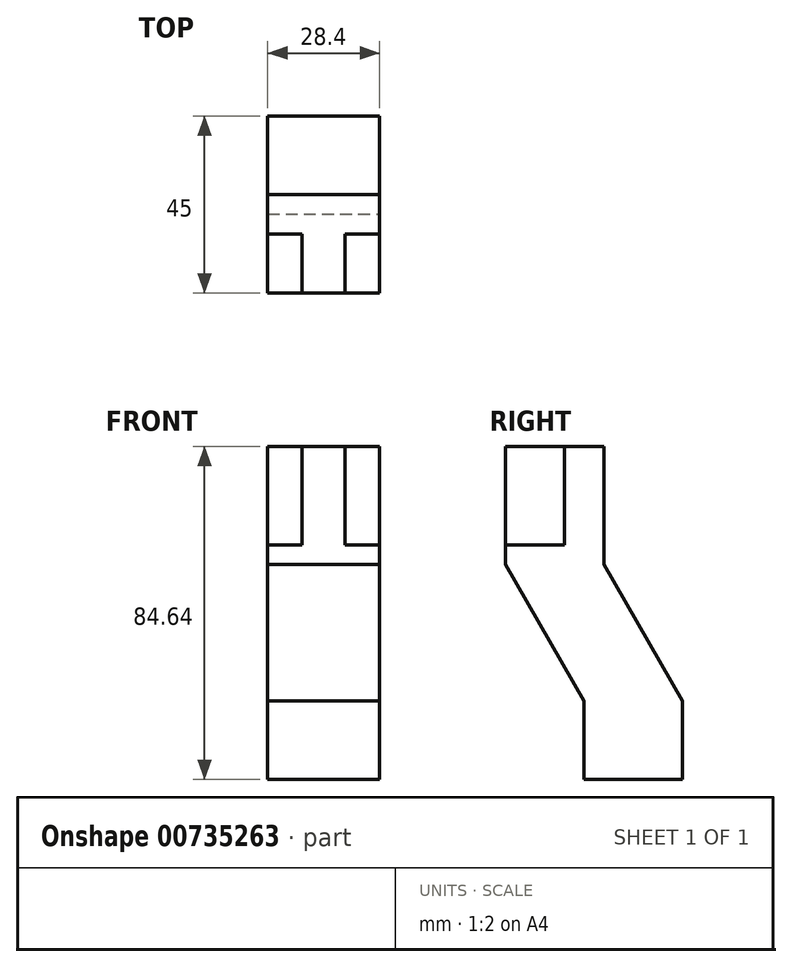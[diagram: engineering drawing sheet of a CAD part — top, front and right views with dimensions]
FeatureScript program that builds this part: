
annotation { "Feature Type Name" : "Feature", "Feature Type Description" : "" }
export const myFeature = defineFeature(function(context is Context, id is Id, definition is map)
    precondition{}
    {
        {
            var Q0;
            Q0=qCreatedBy(makeId("Top.planeOp"),FACE);
            var sketch = newSketch(context, id + "F0", { "sketchPlane" : qUnion([Q0])});
            skLineSegment(sketch, "E0", {"start": v(-5.5, -12.5) * mm, "end": v(5.5, -12.5) * mm});
            skLineSegment(sketch, "E1", {"start": v(5.5, -12.5) * mm, "end": v(5.5, 2.5) * mm});
            skLineSegment(sketch, "E2", {"start": v(5.5, 2.5) * mm, "end": v(14.2, 2.5) * mm});
            skLineSegment(sketch, "E3", {"start": v(14.2, 2.5) * mm, "end": v(14.2, 12.5) * mm});
            skLineSegment(sketch, "E4", {"start": v(14.2, 12.5) * mm, "end": v(-14.2, 12.5) * mm});
            skLineSegment(sketch, "E5", {"start": v(-14.2, 12.5) * mm, "end": v(-14.2, 2.5) * mm});
            skLineSegment(sketch, "E6", {"start": v(-14.2, 2.5) * mm, "end": v(-5.5, 2.5) * mm});
            skLineSegment(sketch, "E7", {"start": v(-5.5, 2.5) * mm, "end": v(-5.5, -12.5) * mm});
            skSolve(sketch);
        }
        {
            var Q0;
            Q0=makeQuery(id+"F0.imprint","IMPRINT",FACE,{"disambiguationData":[TD([[makeQuery(id+"F0.imprint","IMPRINT",EDGE,{"derivedFrom":sQuery(id+"F0.wireOp",EDGE,"E0")}),1.0]])]});
            extrude(context, id + "F1", {"entities" : qUnion([Q0]), "oppositeDirection" : true, "depth" : 25 * mm});
        }
        {
            var Q0;
            Q0=makeQuery(id+"F1.opExtrude","CAP_FACE",FACE,{"disambiguationData":[OSD([sQuery(id+"F0.wireOp",EDGE,"E0"),sQuery(id+"F0.wireOp",EDGE,"E1"),sQuery(id+"F0.wireOp",EDGE,"E2"),sQuery(id+"F0.wireOp",EDGE,"E3"),sQuery(id+"F0.wireOp",EDGE,"E4"),sQuery(id+"F0.wireOp",EDGE,"E5"),sQuery(id+"F0.wireOp",EDGE,"E6"),sQuery(id+"F0.wireOp",EDGE,"E7")])],"isStart":false});
            var sketch = newSketch(context, id + "F2", { "sketchPlane" : qUnion([Q0])});
            skLineSegment(sketch, "E8.bottom", {"start": v(-14.2, 12.5) * mm, "end": v(14.2, 12.5) * mm});
            skLineSegment(sketch, "E8.top", {"start": v(-14.2, -12.5) * mm, "end": v(14.2, -12.5) * mm});
            skLineSegment(sketch, "E8.left", {"start": v(-14.2, 12.5) * mm, "end": v(-14.2, -12.5) * mm});
            skLineSegment(sketch, "E8.right", {"start": v(14.2, 12.5) * mm, "end": v(14.2, -12.5) * mm});
            skSolve(sketch);
        }
        {
            var Q0;
            Q0=qSketchRegion(id+"F2",true);
            extrude(context, id + "F3", {"entities" : qUnion([Q0]), "operationType" : NewBodyOperationType.ADD, "depth" : 5 * mm});
        }
        {
            var Q0;
            Q0=makeQuery(id+"F3.boolean.opBoolean","MERGE",FACE,{"derivedFrom":[makeQuery(id+"F1.opExtrude","SWEPT_FACE",FACE,{"disambiguationData":[OSD([sQuery(id+"F0.wireOp",EDGE,"E3")])]}),makeQuery(id+"F3.opExtrude","SWEPT_FACE",FACE,{"disambiguationData":[OSD([sQuery(id+"F2.wireOp",EDGE,"E8.right")])]})]});
            var sketch = newSketch(context, id + "F4", { "sketchPlane" : qUnion([Q0])});
            skLineSegment(sketch, "E9", {"start": v(12.5, -30) * mm, "end": v(-12.5, -30) * mm});
            skLineSegment(sketch, "E10", {"start": v(-12.5, -30) * mm, "end": v(7.5, -64.64) * mm});
            skLineSegment(sketch, "E11", {"start": v(7.5, -64.64) * mm, "end": v(7.5, -84.64) * mm});
            skLineSegment(sketch, "E12", {"start": v(7.5, -84.64) * mm, "end": v(32.5, -84.64) * mm});
            skLineSegment(sketch, "E13", {"start": v(32.5, -84.64) * mm, "end": v(32.5, -64.64) * mm});
            skLineSegment(sketch, "E14", {"start": v(32.5, -64.64) * mm, "end": v(12.5, -30) * mm});
            skSolve(sketch);
        }
        {
            var Q0;
            Q0=makeQuery(id+"F4.imprint","IMPRINT",FACE,{"disambiguationData":[TD([[makeQuery(id+"F4.imprint","IMPRINT",EDGE,{"derivedFrom":sQuery(id+"F4.wireOp",EDGE,"E9")}),-1.0]])]});
            extrude(context, id + "F5", {"entities" : qUnion([Q0]), "operationType" : NewBodyOperationType.ADD, "oppositeDirection" : true, "depth" : 28.4 * mm});
        }
    });
